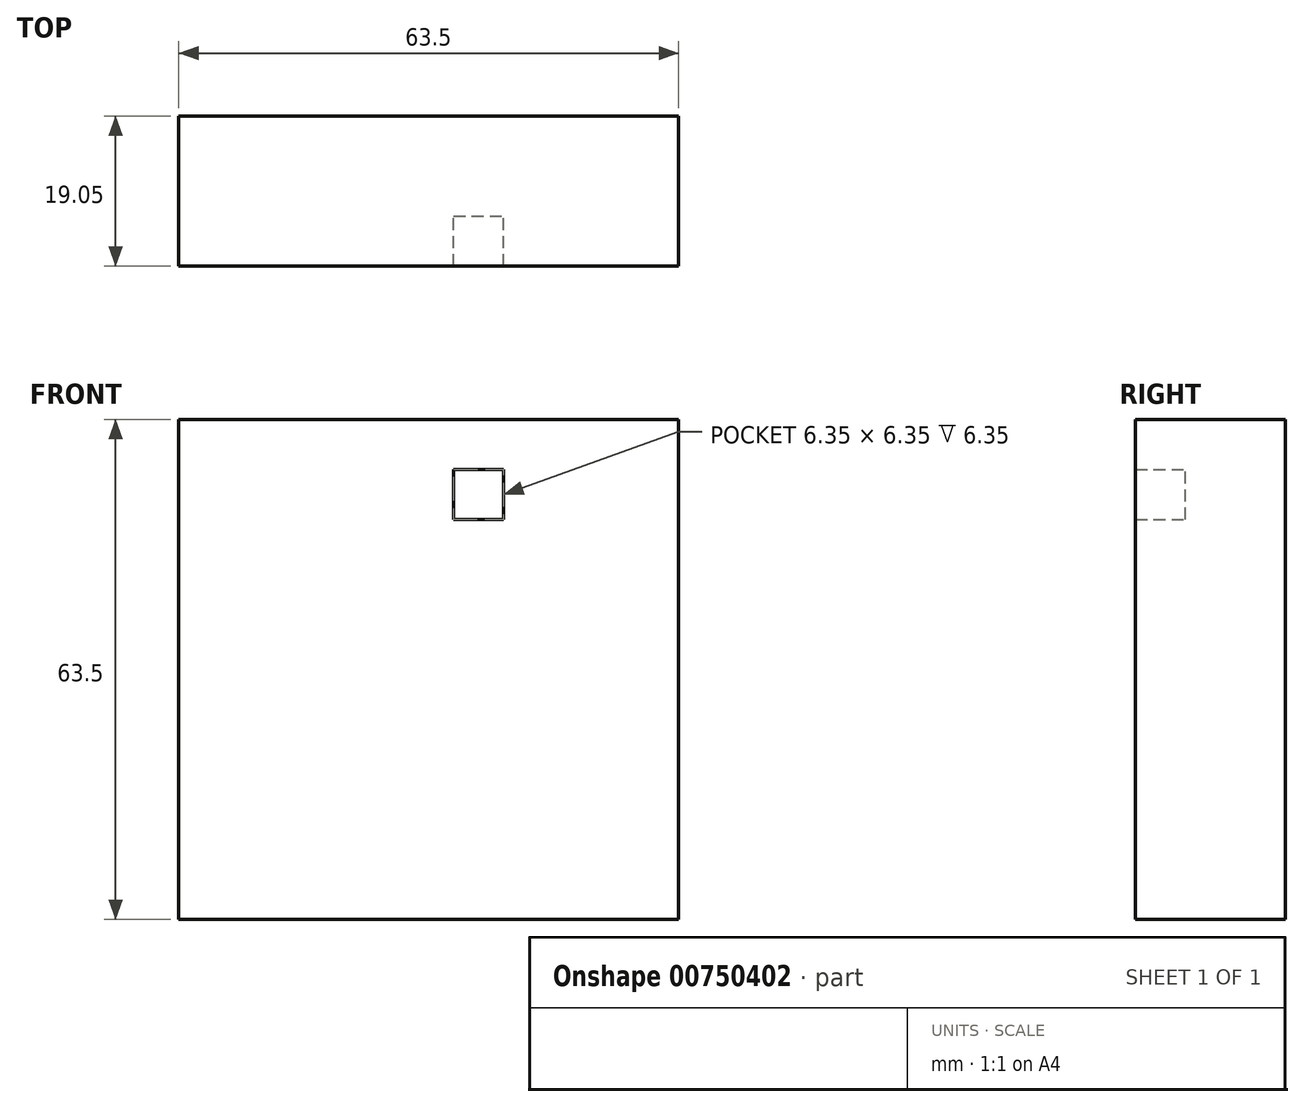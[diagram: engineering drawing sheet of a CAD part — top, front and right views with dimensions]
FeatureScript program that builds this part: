
annotation { "Feature Type Name" : "Feature", "Feature Type Description" : "" }
export const myFeature = defineFeature(function(context is Context, id is Id, definition is map)
    precondition{}
    {
        {
            var Q0;
            Q0=qCreatedBy(makeId("Front.planeOp"),FACE);
            var sketch = newSketch(context, id + "F0", { "sketchPlane" : qUnion([Q0])});
            skLineSegment(sketch, "E0", {"start": v(0, 0) * mm, "end": v(0, 31.48) * mm});
            skLineSegment(sketch, "E1", {"start": v(0, 31.48) * mm, "end": v(-32.02, 31.48) * mm});
            skLineSegment(sketch, "E2", {"start": v(-32.02, 31.48) * mm, "end": v(-32.02, 0) * mm});
            skLineSegment(sketch, "E3", {"start": v(-32.02, 0) * mm, "end": v(0, 0) * mm});
            skLineSegment(sketch, "E4.bottom", {"start": v(-32.02, 31.48) * mm, "end": v(31.48, 31.48) * mm});
            skLineSegment(sketch, "E4.top", {"start": v(-32.02, -32.02) * mm, "end": v(31.48, -32.02) * mm});
            skLineSegment(sketch, "E4.left", {"start": v(-32.02, 31.48) * mm, "end": v(-32.02, -32.02) * mm});
            skLineSegment(sketch, "E4.right", {"start": v(31.48, 31.48) * mm, "end": v(31.48, -32.02) * mm});
            skSolve(sketch);
        }
        {
            var Q0;
            Q0 = qSketchRegion(id + "F0", true);
            var Q1;
            {var subQ0=sQuery(id+"F0.wireOp",EDGE,"E0");Q1=makeQuery(id+"F0.imprint","IMPRINT",FACE,{"disambiguationData":[TD([[makeQuery(id+"F0.imprint","IMPRINT",EDGE,{"derivedFrom":subQ0}),1.0]])]});}
            extrude(context, id + "F1", {"entities" : qUnion([Q0, Q1]), "depth" : 12.7 * mm, "offsetDistance" : 25.4 * mm});
        }
        {
            var Q0;
            Q0=makeQuery(id+"F1.opExtrude","CAP_FACE",FACE,{"disambiguationData":[OSD([sQuery(id+"F0.wireOp",EDGE,"E4.bottom"),sQuery(id+"F0.wireOp",EDGE,"E4.top"),sQuery(id+"F0.wireOp",EDGE,"E4.left"),sQuery(id+"F0.wireOp",EDGE,"E4.right")])],"isStart":false});
            var sketch = newSketch(context, id + "F2", { "sketchPlane" : qUnion([Q0])});
            skLineSegment(sketch, "E5", {"start": v(31.48, 31.48) * mm, "end": v(31.48, -0.27) * mm});
            skLineSegment(sketch, "E6", {"start": v(31.48, -0.27) * mm, "end": v(31.48, 31.48) * mm});
            skLineSegment(sketch, "E7", {"start": v(31.48, 31.48) * mm, "end": v(31.48, 25.13) * mm});
            skLineSegment(sketch, "E8", {"start": v(-32.02, 31.48) * mm, "end": v(-25.67, 31.48) * mm});
            skLineSegment(sketch, "E9", {"start": v(-32.02, 31.48) * mm, "end": v(-32.02, 25.13) * mm});
            skLineSegment(sketch, "E10.bottom", {"start": v(31.48, 31.48) * mm, "end": v(-25.67, 31.48) * mm});
            skLineSegment(sketch, "E10.top", {"start": v(31.48, 25.13) * mm, "end": v(-25.67, 25.13) * mm});
            skLineSegment(sketch, "E10.right", {"start": v(-25.67, 31.48) * mm, "end": v(-25.67, 25.13) * mm});
            skLineSegment(sketch, "E11", {"start": v(-32.02, -32.02) * mm, "end": v(-25.67, -32.02) * mm});
            skLineSegment(sketch, "E12", {"start": v(-25.67, -32.02) * mm, "end": v(-32.02, -32.02) * mm});
            skLineSegment(sketch, "E13", {"start": v(-32.02, -32.02) * mm, "end": v(-32.02, -25.67) * mm});
            skLineSegment(sketch, "E14.bottom", {"start": v(-25.67, 25.13) * mm, "end": v(-19.32, 25.13) * mm});
            skLineSegment(sketch, "E14.top", {"start": v(-25.67, -25.67) * mm, "end": v(-19.32, -25.67) * mm});
            skLineSegment(sketch, "E14.left", {"start": v(-25.67, 25.13) * mm, "end": v(-25.67, -25.67) * mm});
            skLineSegment(sketch, "E14.right", {"start": v(-19.32, 25.13) * mm, "end": v(-19.32, -25.67) * mm});
            skLineSegment(sketch, "E15.bottom", {"start": v(-19.32, -25.67) * mm, "end": v(25.13, -25.67) * mm});
            skLineSegment(sketch, "E15.top", {"start": v(-19.32, -19.32) * mm, "end": v(25.13, -19.32) * mm});
            skLineSegment(sketch, "E15.left", {"start": v(-19.32, -25.67) * mm, "end": v(-19.32, -19.32) * mm});
            skLineSegment(sketch, "E15.right", {"start": v(25.13, -25.67) * mm, "end": v(25.13, -19.32) * mm});
            skLineSegment(sketch, "E16.bottom", {"start": v(25.13, -19.32) * mm, "end": v(18.78, -19.32) * mm});
            skLineSegment(sketch, "E16.top", {"start": v(25.13, 18.78) * mm, "end": v(18.78, 18.78) * mm});
            skLineSegment(sketch, "E16.left", {"start": v(25.13, -19.32) * mm, "end": v(25.13, 18.78) * mm});
            skLineSegment(sketch, "E16.right", {"start": v(18.78, -19.32) * mm, "end": v(18.78, 18.78) * mm});
            skLineSegment(sketch, "E17.bottom", {"start": v(18.78, 18.78) * mm, "end": v(-12.97, 18.78) * mm});
            skLineSegment(sketch, "E17.top", {"start": v(18.78, 12.43) * mm, "end": v(-12.97, 12.43) * mm});
            skLineSegment(sketch, "E17.left", {"start": v(18.78, 18.78) * mm, "end": v(18.78, 12.43) * mm});
            skLineSegment(sketch, "E17.right", {"start": v(-12.97, 18.78) * mm, "end": v(-12.97, 12.43) * mm});
            skLineSegment(sketch, "E18.bottom", {"start": v(-12.97, 12.43) * mm, "end": v(-6.62, 12.43) * mm});
            skLineSegment(sketch, "E18.top", {"start": v(-12.97, -12.97) * mm, "end": v(-6.62, -12.97) * mm});
            skLineSegment(sketch, "E18.left", {"start": v(-12.97, 12.43) * mm, "end": v(-12.97, -12.97) * mm});
            skLineSegment(sketch, "E18.right", {"start": v(-6.62, 12.43) * mm, "end": v(-6.62, -12.97) * mm});
            skLineSegment(sketch, "E19.bottom", {"start": v(-6.62, -12.97) * mm, "end": v(12.43, -12.97) * mm});
            skLineSegment(sketch, "E19.top", {"start": v(-6.62, -6.62) * mm, "end": v(12.43, -6.62) * mm});
            skLineSegment(sketch, "E19.left", {"start": v(-6.62, -12.97) * mm, "end": v(-6.62, -6.62) * mm});
            skLineSegment(sketch, "E19.right", {"start": v(12.43, -12.97) * mm, "end": v(12.43, -6.62) * mm});
            skLineSegment(sketch, "E20.bottom", {"start": v(12.43, -6.62) * mm, "end": v(6.08, -6.62) * mm});
            skLineSegment(sketch, "E20.top", {"start": v(12.43, 6.08) * mm, "end": v(6.08, 6.08) * mm});
            skLineSegment(sketch, "E20.left", {"start": v(12.43, -6.62) * mm, "end": v(12.43, 6.08) * mm});
            skLineSegment(sketch, "E20.right", {"start": v(6.08, -6.62) * mm, "end": v(6.08, 6.08) * mm});
            skLineSegment(sketch, "E21.bottom", {"start": v(6.08, 6.08) * mm, "end": v(-0.27, 6.08) * mm});
            skLineSegment(sketch, "E21.top", {"start": v(6.08, -0.27) * mm, "end": v(-0.27, -0.27) * mm});
            skLineSegment(sketch, "E21.left", {"start": v(6.08, 6.08) * mm, "end": v(6.08, -0.27) * mm});
            skLineSegment(sketch, "E21.right", {"start": v(-0.27, 6.08) * mm, "end": v(-0.27, -0.27) * mm});
            skSolve(sketch);
        }
        {
            var Q0;
            Q0=makeQuery(id+"F2.imprint","IMPRINT",FACE,{"disambiguationData":[TD([[makeQuery(id+"F2.imprint","IMPRINT",EDGE,{"derivedFrom":sQuery(id+"F2.wireOp",EDGE,"E10.bottom")}),-1.0]])]});
            var Q1;
            Q1=makeQuery(id+"F2.imprint","IMPRINT",FACE,{"disambiguationData":[TD([[makeQuery(id+"F2.imprint","IMPRINT",EDGE,{"derivedFrom":sQuery(id+"F2.wireOp",EDGE,"E14.bottom")}),-1.0]])]});
            var Q2;
            Q2=makeQuery(id+"F2.imprint","IMPRINT",FACE,{"disambiguationData":[TD([[makeQuery(id+"F2.imprint","IMPRINT",EDGE,{"derivedFrom":sQuery(id+"F2.wireOp",EDGE,"E15.bottom")}),1.0]])]});
            var Q3;
            Q3=makeQuery(id+"F2.imprint","IMPRINT",FACE,{"disambiguationData":[TD([[makeQuery(id+"F2.imprint","IMPRINT",EDGE,{"derivedFrom":sQuery(id+"F2.wireOp",EDGE,"E16.bottom")}),-1.0]])]});
            var Q4;
            Q4=makeQuery(id+"F2.imprint","IMPRINT",FACE,{"disambiguationData":[TD([[makeQuery(id+"F2.imprint","IMPRINT",EDGE,{"derivedFrom":sQuery(id+"F2.wireOp",EDGE,"E17.bottom")}),1.0]])]});
            var Q5;
            Q5=makeQuery(id+"F2.imprint","IMPRINT",FACE,{"disambiguationData":[TD([[makeQuery(id+"F2.imprint","IMPRINT",EDGE,{"derivedFrom":sQuery(id+"F2.wireOp",EDGE,"E18.bottom")}),-1.0]])]});
            var Q6;
            Q6=makeQuery(id+"F2.imprint","IMPRINT",FACE,{"disambiguationData":[TD([[makeQuery(id+"F2.imprint","IMPRINT",EDGE,{"derivedFrom":sQuery(id+"F2.wireOp",EDGE,"E19.bottom")}),1.0]])]});
            var Q7;
            Q7=makeQuery(id+"F2.imprint","IMPRINT",FACE,{"disambiguationData":[TD([[makeQuery(id+"F2.imprint","IMPRINT",EDGE,{"derivedFrom":sQuery(id+"F2.wireOp",EDGE,"E20.bottom")}),-1.0]])]});
            var Q8;
            Q8=makeQuery(id+"F2.imprint","IMPRINT",FACE,{"disambiguationData":[TD([[makeQuery(id+"F2.imprint","IMPRINT",EDGE,{"derivedFrom":sQuery(id+"F2.wireOp",EDGE,"E21.bottom")}),1.0]])]});
            extrude(context, id + "F3", {"entities" : qUnion([Q0, Q1, Q2, Q3, Q4, Q5, Q6, Q7, Q8]), "operationType" : NewBodyOperationType.ADD, "depth" : 6.35 * mm, "offsetDistance" : 25.4 * mm});
        }
        {
            var Q0;
            Q0=makeQuery(id+"F1.opExtrude","CAP_FACE",FACE,{"disambiguationData":[OSD([sQuery(id+"F0.wireOp",EDGE,"E4.bottom"),sQuery(id+"F0.wireOp",EDGE,"E4.top"),sQuery(id+"F0.wireOp",EDGE,"E4.left"),sQuery(id+"F0.wireOp",EDGE,"E4.right")])],"isStart":false});
            var sketch = newSketch(context, id + "F4", { "sketchPlane" : qUnion([Q0])});
            skLineSegment(sketch, "E22", {"start": v(6.08, 18.78) * mm, "end": v(2.9, 18.78) * mm});
            skLineSegment(sketch, "E23", {"start": v(2.9, 18.78) * mm, "end": v(6.08, 18.78) * mm});
            skLineSegment(sketch, "E24", {"start": v(6.08, 18.78) * mm, "end": v(9.25, 18.78) * mm});
            skLineSegment(sketch, "E25.bottom", {"start": v(2.9, 18.78) * mm, "end": v(9.25, 18.78) * mm});
            skLineSegment(sketch, "E25.top", {"start": v(2.9, 25.13) * mm, "end": v(9.25, 25.13) * mm});
            skLineSegment(sketch, "E25.left", {"start": v(2.9, 18.78) * mm, "end": v(2.9, 25.13) * mm});
            skLineSegment(sketch, "E25.right", {"start": v(9.25, 18.78) * mm, "end": v(9.25, 25.13) * mm});
            skLineSegment(sketch, "E26", {"start": v(-12.97, 2.9) * mm, "end": v(-12.97, 6.08) * mm});
            skLineSegment(sketch, "E27", {"start": v(-12.97, 6.08) * mm, "end": v(-12.97, 2.9) * mm});
            skLineSegment(sketch, "E28", {"start": v(-12.97, 2.9) * mm, "end": v(-12.97, -0.27) * mm});
            skLineSegment(sketch, "E29.bottom", {"start": v(-12.97, 6.08) * mm, "end": v(-19.32, 6.08) * mm});
            skLineSegment(sketch, "E29.top", {"start": v(-12.97, 0) * mm, "end": v(-19.32, 0) * mm});
            skLineSegment(sketch, "E29.left", {"start": v(-12.97, 6.08) * mm, "end": v(-12.97, 0) * mm});
            skLineSegment(sketch, "E29.right", {"start": v(-19.32, 6.08) * mm, "end": v(-19.32, 0) * mm});
            skLineSegment(sketch, "E30", {"start": v(-0.27, -12.97) * mm, "end": v(-3.45, -12.97) * mm});
            skLineSegment(sketch, "E31", {"start": v(-3.45, -12.97) * mm, "end": v(-0.27, -12.97) * mm});
            skLineSegment(sketch, "E32", {"start": v(-0.27, -12.97) * mm, "end": v(2.9, -12.97) * mm});
            skLineSegment(sketch, "E33.bottom", {"start": v(-3.45, -12.97) * mm, "end": v(2.9, -12.97) * mm});
            skLineSegment(sketch, "E33.top", {"start": v(-3.45, -19.32) * mm, "end": v(2.9, -19.32) * mm});
            skLineSegment(sketch, "E33.left", {"start": v(-3.45, -12.97) * mm, "end": v(-3.45, -19.32) * mm});
            skLineSegment(sketch, "E33.right", {"start": v(2.9, -12.97) * mm, "end": v(2.9, -19.32) * mm});
            skLineSegment(sketch, "E34", {"start": v(12.43, -3.45) * mm, "end": v(12.43, -6.62) * mm});
            skLineSegment(sketch, "E35", {"start": v(12.43, -6.62) * mm, "end": v(12.43, -3.45) * mm});
            skLineSegment(sketch, "E36", {"start": v(12.43, -3.45) * mm, "end": v(12.43, -0.27) * mm});
            skLineSegment(sketch, "E37.bottom", {"start": v(12.43, -6.62) * mm, "end": v(18.78, -6.62) * mm});
            skLineSegment(sketch, "E37.top", {"start": v(12.43, -0.27) * mm, "end": v(18.78, -0.27) * mm});
            skLineSegment(sketch, "E37.left", {"start": v(12.43, -6.62) * mm, "end": v(12.43, -0.27) * mm});
            skLineSegment(sketch, "E37.right", {"start": v(18.78, -6.62) * mm, "end": v(18.78, -0.27) * mm});
            skSolve(sketch);
        }
        {
            var Q0;
            Q0=makeQuery(id+"F4.imprint","IMPRINT",FACE,{"disambiguationData":[TD([[makeQuery(id+"F4.imprint","IMPRINT",EDGE,{"derivedFrom":sQuery(id+"F4.wireOp",EDGE,"E25.top")}),1.0]])]});
            var Q1;
            {var subQ0=sQuery(id+"F4.wireOp",EDGE,"E29.bottom");Q1=makeQuery(id+"F4.imprint","IMPRINT",FACE,{"disambiguationData":[TD([[makeQuery(id+"F4.imprint","IMPRINT",EDGE,{"derivedFrom":subQ0}),1.0]])]});}
            var Q2;
            Q2=makeQuery(id+"F4.imprint","IMPRINT",FACE,{"disambiguationData":[TD([[makeQuery(id+"F4.imprint","IMPRINT",EDGE,{"derivedFrom":sQuery(id+"F4.wireOp",EDGE,"E33.top")}),1.0]])]});
            var Q3;
            {var subQ0=sQuery(id+"F4.wireOp",EDGE,"E37.bottom");Q3=makeQuery(id+"F4.imprint","IMPRINT",FACE,{"disambiguationData":[TD([[makeQuery(id+"F4.imprint","IMPRINT",EDGE,{"derivedFrom":subQ0}),1.0]])]});}
            extrude(context, id + "F5", {"entities" : qUnion([Q0, Q1, Q2, Q3]), "operationType" : NewBodyOperationType.ADD, "depth" : 6.35 * mm, "offsetDistance" : 25.4 * mm});
        }
    });
